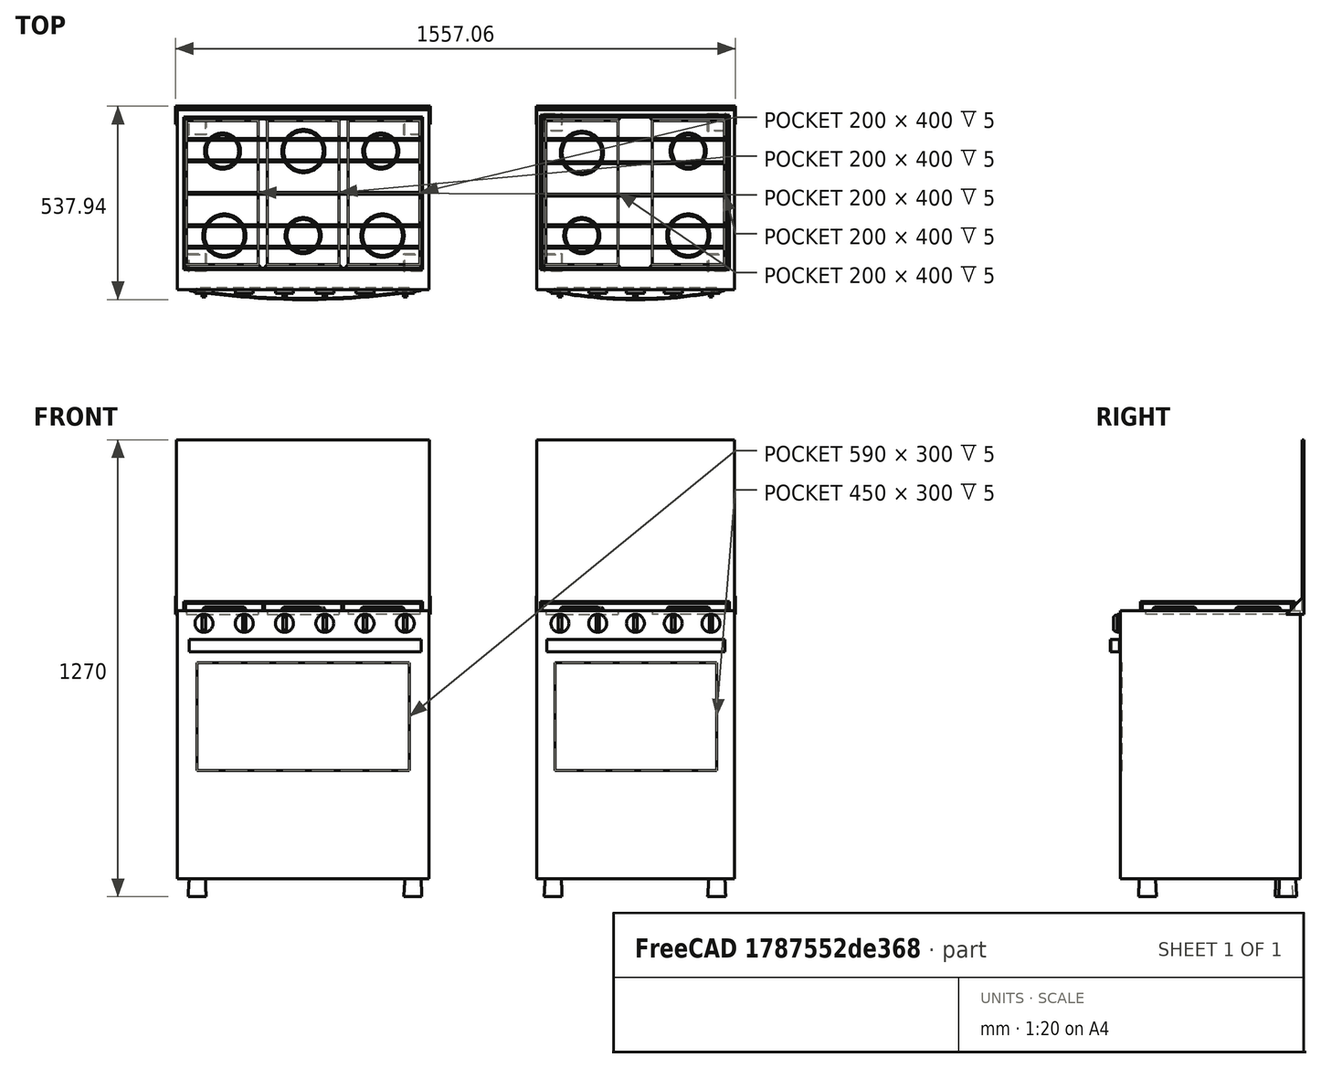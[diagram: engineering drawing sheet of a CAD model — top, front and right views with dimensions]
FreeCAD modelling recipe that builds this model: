
FCSTD DOCUMENT  (FreeCAD 0.16R6706 (Git))
Label: fogao
License: All rights reserved
LicenseURL: http://en.wikipedia.org/wiki/All_rights_reserved
objects: Part::Extrusion×31, Part::Part2DObjectPython×25, Part::FeaturePython×23, Part::MultiFuse×18, Part::Feature×10, Part::Cut×9, Part::Fillet×5, Part::Chamfer×4, Part::Sweep×1, Part::Box×1, Part::Loft×1
note: 128 computed .brp shape members not serialized (recipe doc carries the construction recipe); baked Part::Feature solids carry a one-line shape summary decoded from their .brp

FEATURE [Part::Part2DObjectPython] Rectangle  # Draft 2D object (typed FeaturePython)
  ChamferSize = 0
  Columns = 1
  FilletRadius = 0
  Height = -500
  Length = 550
  MakeFace = true
  Placement = pos=(500,300,50) rot=(0,0,1;0rad)
  Rows = 1
FEATURE [Part::Extrusion] Extrusion
  Base = -> Rectangle
  Dir = (0,0,250)
  Solid = true
FEATURE [Part::Feature] Face
  Placement = pos=(500,300,300) rot=(0,0,1;0rad)
  shape: bbox 550 x 500 x 2e-07 mm, 1 faces, 0 solids (baked)
FEATURE [Part::Extrusion] Extrusion001
  Base = -> Face
  Dir = (0,0,425)
  Solid = true
FEATURE [Part::Feature] Clone001  label="Clone of Solid002"
  Placement = pos=(775,0,10) rot=(0,0,1;0rad)
  shape: bbox 554 x 50 x 485 mm, 16 faces (baked)
FEATURE [Part::Feature] Face310
  Placement = pos=(500,300,725) rot=(0,0,1;0rad)
  shape: bbox 550 x 500 x 2e-07 mm, 1 faces, 0 solids (baked)
FEATURE [Part::Extrusion] Extrusion002
  Base = -> Face310
  Dir = (0,0,70)
  Solid = true
FEATURE [Part::Part2DObjectPython] Rectangle001  # Draft 2D object (typed FeaturePython)
  ChamferSize = 0
  Columns = 1
  FilletRadius = 0
  Height = -35
  Length = 3
  MakeFace = true
  Placement = pos=(525,-200,715) rot=(0.57735,-0.57735,-0.57735;2.0944rad)
  Rows = 1
  Support = -> Extrusion001
FEATURE [Part::Sweep] Sweep
  Frenet = false
  Placement = pos=(2,0,0) rot=(0,0,1;0rad)
  Sections = -> [Rectangle001]
  Solid = true
  Transition = 1
FEATURE [Part::Part2DObjectPython] Circle  # Draft 2D object (typed FeaturePython)
  FirstAngle = 0
  LastAngle = 0
  MakeFace = true
  Placement = pos=(574.102,-200,757.714) rot=(1,0,0;1.5708rad)
  Radius = 25
FEATURE [Part::Extrusion] Extrusion003
  Base = -> Circle
  Dir = (0,-10,0)
  Solid = true
FEATURE [Part::FeaturePython] Clone002  label="Clone of Chamfer001"  # WARN: FeaturePython — macro-defined, semantics opaque (R4)
  Placement = pos=(-430.898,180,808.25) rot=(0,0,1;0rad)
  Scale = (1,1,0.9)
FEATURE [Part::MultiFuse] Fusion
  Placement = pos=(0,0,2) rot=(0,0,1;0rad)
  Shapes = -> [Extrusion003,Clone002]
FEATURE [Part::FeaturePython] Array  # Draft array (typed FeaturePython)
  Angle = 360
  ArrayType = 0
  Axis = (0,0,1)
  Base = -> Fusion
  Center = (0,0,0)
  Fuse = false
  IntervalAxis = (0,0,0)
  IntervalX = (105,0,0)
  IntervalY = (0,1,0)
  IntervalZ = (0,0,0)
  NumberPolar = 1
  NumberX = 5
  NumberY = 2
  NumberZ = 1
  Placement = pos=(-10,0,0) rot=(0,0,1;0rad)
FEATURE [Part::Part2DObjectPython] Rectangle002  # Draft 2D object (typed FeaturePython)
  ChamferSize = 0
  Columns = 1
  FilletRadius = 0
  Height = -550
  Length = -40
  MakeFace = true
  Placement = pos=(1050,-200,300) rot=(0,0,-1;1.5708rad)
  Rows = 1
FEATURE [Part::Extrusion] Extrusion004
  Base = -> Rectangle002
  Dir = (0,0,425)
  Solid = true
FEATURE [Part::Cut] Cut
  Base = -> Extrusion001
  Tool = -> Extrusion004
FEATURE [Part::Feature] Face311
  shape: bbox 550 x 2e-07 x 425 mm, 1 faces, 0 solids (baked)
FEATURE [Part::Extrusion] Extrusion005
  Base = -> Face311
  Dir = (0,-40,0)
  Solid = true
FEATURE [Part::Part2DObjectPython] Rectangle003  # Draft 2D object (typed FeaturePython)
  ChamferSize = 0
  Columns = 1
  FilletRadius = 0
  Height = 400
  Length = 200
  MakeFace = true
  Placement = pos=(525,-130,795) rot=(0,0,1;0rad)
  Rows = 1
FEATURE [Part::Part2DObjectPython] Circle001  # Draft 2D object (typed FeaturePython)
  FirstAngle = 0
  LastAngle = 0
  MakeFace = true
  Placement = pos=(625,-50,795) rot=(0,0,1;0rad)
  Radius = 50
FEATURE [Part::Part2DObjectPython] Circle002  # Draft 2D object (typed FeaturePython)
  FirstAngle = 0
  LastAngle = 0
  MakeFace = true
  Placement = pos=(625,180,795) rot=(0,0,1;0rad)
  Radius = 60
FEATURE [Part::Feature] mirror001  label="Mirror of Clone of Rectangle003 (2D)001"
  Placement = pos=(295.899,0,795) rot=(0,0,1;0rad)
  shape: bbox 200 x 400 x 2e-07 mm, 1 faces, 0 solids (baked)
FEATURE [Part::Feature] Clone2D004  label="Clone of Circle001 (2D)001"
  Placement = pos=(920.899,-50,795) rot=(0,0,1;0rad)
  shape: bbox 100 x 100 x 2e-07 mm, 1 faces, 0 solids (baked)
FEATURE [Part::Feature] Clone2D005  label="Clone of Circle002 (2D)001"
  Placement = pos=(920.899,180,795) rot=(0,0,1;0rad)
  shape: bbox 120 x 120 x 2e-07 mm, 1 faces, 0 solids (baked)
FEATURE [Part::Extrusion] Extrusion006
  Base = -> Rectangle003
  Dir = (0,0,-10)
  Solid = true
FEATURE [Part::Extrusion] Extrusion007
  Base = -> mirror001
  Dir = (0,0,-10)
  Solid = true
FEATURE [Part::Cut] Cut001
  Base = -> Extrusion002
  Tool = -> Extrusion006
FEATURE [Part::Cut] Cut002
  Base = -> Cut001
  Tool = -> Extrusion007
FEATURE [Part::Extrusion] Extrude
  Base = -> Circle001
  Dir = (0,0,10)
  Solid = false
FEATURE [Part::Extrusion] Extrude001
  Base = -> Circle002
  Dir = (0,0,10)
  Solid = false
FEATURE [Part::Extrusion] Extrude002
  Base = -> Clone2D005
  Dir = (0,0,10)
  Solid = false
FEATURE [Part::Extrusion] Extrude003
  Base = -> Clone2D004
  Dir = (0,0,10)
  Solid = false
FEATURE [Part::Chamfer] Chamfer
  Base = -> Extrude
  Edges = 1 edges r=5: [Edge3]
FEATURE [Part::Chamfer] Chamfer001
  Base = -> Extrude003
  Edges = 1 edges r=5: [Edge3]
  Placement = pos=(0,235,0) rot=(0,0,1;0rad)
FEATURE [Part::Chamfer] Chamfer002
  Base = -> Extrude002
  Edges = 1 edges r=5: [Edge3]
  Placement = pos=(0,-230,0) rot=(0,0,1;0rad)
FEATURE [Part::Chamfer] Chamfer003
  Base = -> Extrude001
  Edges = 1 edges r=5: [Edge3]
FEATURE [Part::Box] Box  label="Cube"
  Height = 25
  Length = 5
  Placement = pos=(510,-145,795) rot=(0,0,1;0rad)
  Width = 5
FEATURE [Part::FeaturePython] Array001  # Draft array (typed FeaturePython)
  Angle = 360
  ArrayType = 0
  Axis = (0,0,1)
  Base = -> Box
  Center = (0,0,0)
  Fuse = false
  IntervalAxis = (0,0,0)
  IntervalX = (520,0,0)
  IntervalY = (0,425,0)
  IntervalZ = (0,0,0)
  NumberPolar = 1
  NumberX = 2
  NumberY = 2
  NumberZ = 1
FEATURE [Part::Part2DObjectPython] Rectangle004  # Draft 2D object (typed FeaturePython)
  ChamferSize = 0
  Columns = 1
  FilletRadius = 0
  Height = 5
  Length = 5
  MakeFace = true
  Placement = pos=(515,-140,820) rot=(0.57735,-0.57735,0.57735;4.18879rad)
  Rows = 1
  Support = -> Array001
FEATURE [Part::Extrusion] Extrusion008
  Base = -> Rectangle004
  Dir = (515,0,0)
  Solid = true
FEATURE [Part::Part2DObjectPython] Rectangle005  # Draft 2D object (typed FeaturePython)
  ChamferSize = 0
  Columns = 1
  FilletRadius = 0
  Height = 5
  Length = 5
  MakeFace = true
  Placement = pos=(515,285,820) rot=(0.57735,-0.57735,0.57735;4.18879rad)
  Rows = 1
  Support = -> Array001
FEATURE [Part::Extrusion] Extrusion009
  Base = -> Rectangle005
  Dir = (515,0,0)
  Solid = true
FEATURE [Part::Part2DObjectPython] Rectangle006  # Draft 2D object (typed FeaturePython)
  ChamferSize = 0
  Columns = 1
  FilletRadius = 0
  Height = 5
  Length = 5
  MakeFace = true
  Placement = pos=(515,280,820) rot=(0,0.707107,-0.707107;3.14159rad)
  Rows = 1
FEATURE [Part::Extrusion] Extrusion010
  Base = -> Rectangle006
  Dir = (0,-420,0)
  Solid = true
FEATURE [Part::Part2DObjectPython] Rectangle007  # Draft 2D object (typed FeaturePython)
  ChamferSize = 0
  Columns = 1
  FilletRadius = 0
  Height = 5
  Length = 5
  MakeFace = true
  Placement = pos=(1035,280,820) rot=(0,0.707107,-0.707107;3.14159rad)
  Rows = 1
  Support = -> Array001
FEATURE [Part::Extrusion] Extrusion011
  Base = -> Rectangle007
  Dir = (0,-420,0)
  Solid = true
FEATURE [Part::FeaturePython] Array002  # Draft array (typed FeaturePython)
  Angle = 360
  ArrayType = 0
  Axis = (0,0,1)
  Base = -> Extrusion008
  Center = (0,0,0)
  Fuse = false
  IntervalAxis = (0,0,0)
  IntervalX = (1,0,0)
  IntervalY = (0,60,0)
  IntervalZ = (0,0,0)
  NumberPolar = 1
  NumberX = 1
  NumberY = 3
  NumberZ = 1
FEATURE [Part::FeaturePython] Array003  # Draft array (typed FeaturePython)
  Angle = 360
  ArrayType = 0
  Axis = (0,0,1)
  Base = -> Extrusion009
  Center = (0,0,0)
  Fuse = false
  IntervalAxis = (0,0,0)
  IntervalX = (1,0,0)
  IntervalY = (0,-65,0)
  IntervalZ = (0,0,0)
  NumberPolar = 1
  NumberX = 2
  NumberY = 3
  NumberZ = 1
FEATURE [Part::FeaturePython] Clone  label="Clone of Extrusion008"  # Draft clone (typed FeaturePython)
  Objects = -> [Extrusion008]
  Placement = pos=(0,205,0) rot=(0,0,1;0rad)
  Scale = (1,1,1)
FEATURE [Part::Fillet] Fillet
  Base = -> Cut002
  Edges = 4 edges r=5: [Edge17,Edge18,Edge19,Edge20]
FEATURE [Part::Fillet] Fillet001
  Base = -> Fillet
  Edges = 4 edges r=5: [Edge9,Edge10,Edge11,Edge12]
FEATURE [Part::Part2DObjectPython] Rectangle008  # Draft 2D object (typed FeaturePython)
  ChamferSize = 0
  Columns = 1
  FilletRadius = 0
  Height = -50
  Length = 50
  MakeFace = true
  Placement = pos=(500,-300,0) rot=(0,0,1;0rad)
  Rows = 1
FEATURE [Part::Part2DObjectPython] Clone2D006  label="Clone of Rectangle008 (2D)"  # Draft 2D object (typed FeaturePython)
  Objects = -> [Rectangle008]
  Placement = pos=(553,-333,50) rot=(0,0,1;0rad)
  Scale = (0.9,0.9,1)
FEATURE [Part::Loft] Loft
  Closed = false
  Placement = pos=(20,200,0) rot=(0,0,1;0rad)
  Ruled = false
  Sections = -> [Rectangle008,Clone2D006]
  Solid = true
FEATURE [Part::FeaturePython] Array004  # Draft array (typed FeaturePython)
  Angle = 360
  ArrayType = 0
  Axis = (0,0,1)
  Base = -> Loft
  Center = (0,0,0)
  Fuse = false
  IntervalAxis = (0,0,0)
  IntervalX = (455,0,0)
  IntervalY = (0,390,0)
  IntervalZ = (0,0,0)
  NumberPolar = 1
  NumberX = 2
  NumberY = 2
  NumberZ = 1
FEATURE [Part::Part2DObjectPython] Rectangle009  # Draft 2D object (typed FeaturePython)
  ChamferSize = 0
  Columns = 1
  FilletRadius = 0
  Height = -300
  Length = -450
  MakeFace = true
  Placement = pos=(1000,-200,650) rot=(1,0,0;1.5708rad)
  Rows = 1
FEATURE [Part::Extrusion] Extrusion012
  Base = -> Rectangle009
  Dir = (0,5,0)
  Solid = true
FEATURE [Part::Cut] Cut003
  Base = -> Extrusion005
  Tool = -> Extrusion012
FEATURE [Part::Part2DObjectPython] Rectangle010  # Draft 2D object (typed FeaturePython)
  ChamferSize = 0
  Columns = 1
  FilletRadius = 0
  Height = -500
  Length = 700
  MakeFace = true
  Placement = pos=(-500,300,50) rot=(0,0,1;0rad)
  Rows = 1
FEATURE [Part::Extrusion] Extrusion013
  Base = -> Rectangle010
  Dir = (0,0,250)
  Solid = true
FEATURE [Part::Feature] Face312
  Placement = pos=(-500,300,300) rot=(0,0,1;0rad)
  shape: bbox 700 x 500 x 2e-07 mm, 1 faces, 0 solids (baked)
FEATURE [Part::Extrusion] Extrusion014
  Base = -> Face312
  Dir = (0,0,425)
  Solid = true
FEATURE [Part::Feature] Face313
  Placement = pos=(-500,300,725) rot=(0,0,1;0rad)
  shape: bbox 700 x 500 x 2e-07 mm, 1 faces, 0 solids (baked)
FEATURE [Part::Extrusion] Extrusion015
  Base = -> Face313
  Dir = (0,0,70)
  Solid = true
FEATURE [Part::Part2DObjectPython] Rectangle011  # Draft 2D object (typed FeaturePython)
  ChamferSize = 0
  Columns = 1
  FilletRadius = 0
  Height = 425
  Length = 700
  MakeFace = true
  Placement = pos=(-500,-200,300) rot=(1,0,0;1.5708rad)
  Rows = 1
  Support = -> Extrusion014
FEATURE [Part::Extrusion] Extrusion016
  Base = -> Rectangle011
  Dir = (0,40,0)
  Solid = true
FEATURE [Part::Cut] Cut004
  Base = -> Extrusion014
  Tool = -> Extrusion016
FEATURE [Part::Feature] Face314
  shape: bbox 700 x 2e-07 x 425 mm, 1 faces, 0 solids (baked)
FEATURE [Part::Extrusion] Extrusion017
  Base = -> Face314
  Dir = (0,-40,0)
  Solid = true
FEATURE [Part::Part2DObjectPython] Rectangle013  # Draft 2D object (typed FeaturePython)
  ChamferSize = 0
  Columns = 1
  FilletRadius = 0
  Height = 200
  Length = 400
  MakeFace = true
  Placement = pos=(-475,270,795) rot=(0,0,-1;1.5708rad)
  Rows = 1
FEATURE [Part::Part2DObjectPython] Rectangle014  # Draft 2D object (typed FeaturePython)
  ChamferSize = 0
  Columns = 1
  FilletRadius = 0
  Height = 200
  Length = 400
  MakeFace = true
  Placement = pos=(-250,270,795) rot=(0,0,-1;1.5708rad)
  Rows = 1
FEATURE [Part::Part2DObjectPython] Rectangle015  # Draft 2D object (typed FeaturePython)
  ChamferSize = 0
  Columns = 1
  FilletRadius = 0
  Height = 200
  Length = 400
  MakeFace = true
  Placement = pos=(-25,270,795) rot=(0,0,-1;1.5708rad)
  Rows = 1
FEATURE [Part::Extrusion] Extrusion018
  Base = -> Rectangle013
  Dir = (0,0,-10)
  Solid = true
FEATURE [Part::Extrusion] Extrusion019
  Base = -> Rectangle014
  Dir = (0,0,-10)
  Solid = true
FEATURE [Part::Extrusion] Extrusion020
  Base = -> Rectangle015
  Dir = (0,0,-10)
  Solid = true
FEATURE [Part::Cut] Cut005
  Base = -> Extrusion015
  Tool = -> Extrusion018
FEATURE [Part::Cut] Cut006
  Base = -> Cut005
  Tool = -> Extrusion019
FEATURE [Part::Cut] Cut007
  Base = -> Cut006
  Tool = -> Extrusion020
FEATURE [Part::FeaturePython] Clone003  label="Clone of Chamfer"  # Draft clone (typed FeaturePython)
  Objects = -> [Chamfer]
  Placement = pos=(-775,0,0) rot=(0,0,1;0rad)
  Scale = (1,1,1)
FEATURE [Part::FeaturePython] Clone004  label="Clone of Chamfer002"  # Draft clone (typed FeaturePython)
  Objects = -> [Chamfer001]
  Placement = pos=(-1295,235,0) rot=(0,0,1;0rad)
  Scale = (1,1,1)
FEATURE [Part::FeaturePython] Clone005  label="Clone of Chamfer003"  # Draft clone (typed FeaturePython)
  Objects = -> [Chamfer002]
  Placement = pos=(-850,-230,0) rot=(0,0,1;0rad)
  Scale = (1,1,1)
FEATURE [Part::FeaturePython] Clone006  label="Clone of Clone of Chamfer002"  # Draft clone (typed FeaturePython)
  Objects = -> [Clone004]
  Placement = pos=(-855,235,0) rot=(0,0,1;0rad)
  Scale = (1,1,1)
FEATURE [Part::FeaturePython] Clone007  label="Clone of Clone of Chamfer003"  # Draft clone (typed FeaturePython)
  Objects = -> [Clone005]
  Placement = pos=(-1290,-230,0) rot=(0,0,1;0rad)
  Scale = (1,1,1)
FEATURE [Part::FeaturePython] Clone008  label="Clone of Clone of Clone of Chamfer003"  # Draft clone (typed FeaturePython)
  Objects = -> [Clone007]
  Placement = pos=(-1070,5,0) rot=(0,0,1;0rad)
  Scale = (1,1,1)
FEATURE [Part::FeaturePython] Clone009  label="Clone of Fusion"  # Draft clone (typed FeaturePython)
  Objects = -> [Fusion]
  Placement = pos=(-1000,0,2) rot=(0,0,1;0rad)
  Scale = (1,1,1)
FEATURE [Part::FeaturePython] Array005  # Draft array (typed FeaturePython)
  Angle = 360
  ArrayType = 0
  Axis = (0,0,1)
  Base = -> Clone009
  Center = (0,0,0)
  Fuse = false
  IntervalAxis = (0,0,0)
  IntervalX = (112,0,0)
  IntervalY = (0,1,0)
  IntervalZ = (0,0,0)
  NumberPolar = 1
  NumberX = 6
  NumberY = 1
  NumberZ = 1
FEATURE [Part::FeaturePython] Clone010  label="Clone of Sweep"  # Draft clone (typed FeaturePython)
  Objects = -> [Sweep]
  Placement = pos=(-1150,0,0) rot=(0,0,1;0rad)
  Scale = (1.3,1,1)
FEATURE [Part::FeaturePython] Clone011  label="Clone of Loft"  # Draft clone (typed FeaturePython)
  Objects = -> [Loft]
  Placement = pos=(-970,200,0) rot=(0,0,1;0rad)
  Scale = (1,1,1)
FEATURE [Part::FeaturePython] Array006  # Draft array (typed FeaturePython)
  Angle = 360
  ArrayType = 0
  Axis = (0,0,1)
  Base = -> Clone011
  Center = (0,0,0)
  Fuse = false
  IntervalAxis = (0,0,0)
  IntervalX = (600,0,0)
  IntervalY = (0,380,0)
  IntervalZ = (0,0,0)
  NumberPolar = 1
  NumberX = 2
  NumberY = 2
  NumberZ = 1
FEATURE [Part::FeaturePython] Clone012  label="Clone of Clone of Solid002"  # Draft clone (typed FeaturePython)
  Objects = -> [Clone001]
  Placement = pos=(-367.5,0,10) rot=(0,0,1;0rad)
  Scale = (1.28,1,1)
FEATURE [Part::Part2DObjectPython] Rectangle016  # Draft 2D object (typed FeaturePython)
  ChamferSize = 0
  Columns = 1
  FilletRadius = 0
  Height = 5
  Length = 5
  MakeFace = true
  Placement = pos=(-500,-500,0) rot=(0,0,1;0rad)
  Rows = 1
FEATURE [Part::Extrusion] Extrude004
  Base = -> Rectangle016
  Dir = (0,0,25)
  Placement = pos=(17.5,355,795) rot=(0,0,1;0rad)
  Solid = true
FEATURE [Part::FeaturePython] Array007  # Draft array (typed FeaturePython)
  Angle = 360
  ArrayType = 0
  Axis = (0,0,1)
  Base = -> Extrude004
  Center = (0,0,0)
  Fuse = false
  IntervalAxis = (0,0,0)
  IntervalX = (220,0,0)
  IntervalY = (0,420,0)
  IntervalZ = (0,0,0)
  NumberPolar = 1
  NumberX = 4
  NumberY = 2
  NumberZ = 1
FEATURE [Part::Part2DObjectPython] Rectangle017  # Draft 2D object (typed FeaturePython)
  ChamferSize = 0
  Columns = 1
  FilletRadius = 0
  Height = -5
  Length = -5
  MakeFace = true
  Placement = pos=(-477.5,-140,820) rot=(0.57735,0.57735,0.57735;2.0944rad)
  Rows = 1
  Support = -> Array007
FEATURE [Part::Extrusion] Extrusion021
  Base = -> Rectangle017
  Dir = (655,0,0)
  Solid = true
FEATURE [Part::Part2DObjectPython] Rectangle018  # Draft 2D object (typed FeaturePython)
  ChamferSize = 0
  Columns = 1
  FilletRadius = 0
  Height = -5
  Length = -5
  MakeFace = true
  Placement = pos=(-477.5,280,820) rot=(0.57735,0.57735,0.57735;2.0944rad)
  Rows = 1
  Support = -> Array007
FEATURE [Part::Extrusion] Extrusion022
  Base = -> Rectangle018
  Dir = (655,0,0)
  Solid = true
FEATURE [Part::Part2DObjectPython] Rectangle019  # Draft 2D object (typed FeaturePython)
  ChamferSize = 0
  Columns = 1
  FilletRadius = 0
  Height = -5
  Length = 5
  MakeFace = true
  Placement = pos=(-482.5,275,820) rot=(1,0,0;1.5708rad)
  Rows = 1
FEATURE [Part::Extrusion] Extrusion023
  Base = -> Rectangle019
  Dir = (0,-415,0)
  Solid = true
FEATURE [Part::Part2DObjectPython] Rectangle020  # Draft 2D object (typed FeaturePython)
  ChamferSize = 0
  Columns = 1
  FilletRadius = 0
  Height = -5
  Length = -5
  MakeFace = true
  Placement = pos=(182.5,275,820) rot=(1,0,0;1.5708rad)
  Rows = 1
  Support = -> Array007
FEATURE [Part::Extrusion] Extrusion024
  Base = -> Rectangle020
  Dir = (0,-415,0)
  Solid = true
FEATURE [Part::FeaturePython] Array008  # Draft array (typed FeaturePython)
  Angle = 360
  ArrayType = 0
  Axis = (0,0,1)
  Base = -> Extrusion021
  Center = (0,0,0)
  Fuse = false
  IntervalAxis = (0,0,0)
  IntervalX = (1,0,0)
  IntervalY = (0,60,0)
  IntervalZ = (0,0,0)
  NumberPolar = 1
  NumberX = 1
  NumberY = 3
  NumberZ = 1
FEATURE [Part::FeaturePython] Array009  # Draft array (typed FeaturePython)
  Angle = 360
  ArrayType = 0
  Axis = (0,0,1)
  Base = -> Extrusion022
  Center = (0,0,0)
  Fuse = false
  IntervalAxis = (0,0,0)
  IntervalX = (1,0,0)
  IntervalY = (0,-60,0)
  IntervalZ = (0,0,0)
  NumberPolar = 1
  NumberX = 1
  NumberY = 3
  NumberZ = 1
FEATURE [Part::FeaturePython] Clone013  label="Clone of Extrusion021"  # Draft clone (typed FeaturePython)
  Objects = -> [Extrusion021]
  Placement = pos=(0,210,0) rot=(0,0,1;0rad)
  Scale = (1,1,1)
FEATURE [Part::Part2DObjectPython] Rectangle021  # Draft 2D object (typed FeaturePython)
  ChamferSize = 0
  Columns = 1
  FilletRadius = 0
  Height = -300
  Length = -590
  MakeFace = true
  Placement = pos=(145,-200,650) rot=(1,0,0;1.5708rad)
  Rows = 1
FEATURE [Part::Extrusion] Extrusion025
  Base = -> Rectangle021
  Dir = (0,5,0)
  Solid = true
FEATURE [Part::Cut] Cut008
  Base = -> Extrusion017
  Tool = -> Extrusion025
FEATURE [Part::MultiFuse] Fusion001
  Shapes = -> [Cut004,Cut008,Extrusion013,Array006]
FEATURE [Part::MultiFuse] Fusion002
  Shapes = -> [Fusion001,Clone010,Array005,Cut007]
FEATURE [Part::MultiFuse] Fusion003
  Shapes = -> [Clone003,Clone004,Clone005,Clone006,Clone007,Clone008,Fusion002]
FEATURE [Part::MultiFuse] Fusion004
  Shapes = -> [Fusion003,Array007]
FEATURE [Part::MultiFuse] Fusion005
  Shapes = -> [Fusion004,Extrusion023,Extrusion024]
FEATURE [Part::MultiFuse] Fusion006
  Shapes = -> [Fusion005,Array008,Array009,Clone013]
FEATURE [Part::MultiFuse] Fusion007
  Shapes = -> [Clone012,Fusion006]
FEATURE [Part::MultiFuse] Fusion008
  Shapes = -> [Fillet001,Cut003]
FEATURE [Part::MultiFuse] Fusion009
  Shapes = -> [Fusion008,Sweep]
FEATURE [Part::MultiFuse] Fusion010
  Shapes = -> [Extrusion,Fusion009]
FEATURE [Part::MultiFuse] Fusion011
  Shapes = -> [Cut,Fusion010]
FEATURE [Part::MultiFuse] Fusion012
  Shapes = -> [Array004,Fusion011]
FEATURE [Part::MultiFuse] Fusion013
  Shapes = -> [Clone001,Fusion012]
FEATURE [Part::MultiFuse] Fusion014
  Shapes = -> [Array,Fusion013]
FEATURE [Part::MultiFuse] Fusion015
  Shapes = -> [Array001,Fusion014]
FEATURE [Part::MultiFuse] Fusion016
  Shapes = -> [Chamfer,Chamfer001,Chamfer002,Chamfer003,Fusion015]
FEATURE [Part::MultiFuse] Fusion017  label="fog4"
  Shapes = -> [Extrusion010,Extrusion011,Array002,Array003,Clone,Fusion016]
FEATURE [Part::Fillet] Fillet002
  Base = -> Fusion007
  Edges = 4 edges r=5: [Edge91,Edge92,Edge93,Edge94]
FEATURE [Part::Fillet] Fillet003
  Base = -> Fillet002
  Edges = 4 edges r=5: [Edge18,Edge19,Edge20,Edge21]
FEATURE [Part::Fillet] Fillet004  label="fog6"
  Base = -> Fillet003
  Edges = 4 edges r=5: [Edge34,Edge35,Edge36,Edge37]
